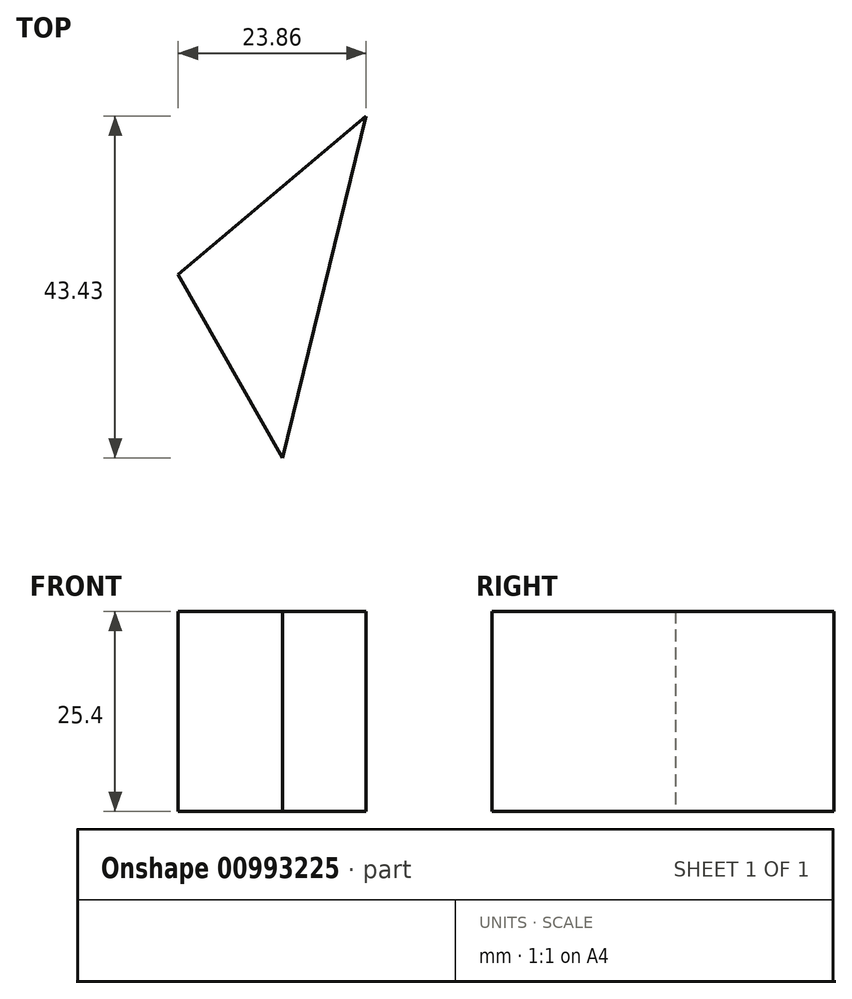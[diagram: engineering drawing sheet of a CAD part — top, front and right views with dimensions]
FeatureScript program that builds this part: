
annotation { "Feature Type Name" : "Feature", "Feature Type Description" : "" }
export const myFeature = defineFeature(function(context is Context, id is Id, definition is map)
    precondition{}
    {
        {
            var Q0;
            Q0=qCreatedBy(makeId("Top.planeOp"),FACE);
            var sketch = newSketch(context, id + "F0", { "sketchPlane" : qUnion([Q0])});
            skLineSegment(sketch, "E0", {"start": v(0, 0) * mm, "end": v(-23.86, -20.14) * mm});
            skLineSegment(sketch, "E1", {"start": v(-23.86, -20.14) * mm, "end": v(-10.64, -43.43) * mm});
            skLineSegment(sketch, "E2", {"start": v(-10.64, -43.43) * mm, "end": v(0, 0) * mm});
            skSolve(sketch);
        }
        {
            var Q0;
            Q0=makeQuery(id+"F0.imprint","IMPRINT",FACE,{"disambiguationData":[TD([[makeQuery(id+"F0.imprint","IMPRINT",EDGE,{"derivedFrom":sQuery(id+"F0.wireOp",EDGE,"E0")}),1.0]])]});
            extrude(context, id + "F1", {"entities" : qUnion([Q0]), "depth" : 25.4 * mm, "offsetDistance" : 25.4 * mm});
        }
    });
